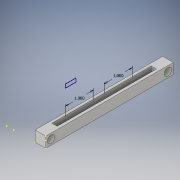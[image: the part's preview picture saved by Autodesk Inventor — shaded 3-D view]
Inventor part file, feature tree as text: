
AUTODESK INVENTOR PART (.ipt)
format: ipt  version: 2018 (Build 220112000, 112)  size: 350,208 bytes
history: native  units: in
note: dims shown in document units (in); Inventor stores cm internally (conversion verified against a paired STEP export)
features: sketch x21, extrude x11, fillet x2, hole x1
ambient origin geometry x8: Origin, YZ Plane, XZ Plane, XY Plane, X Axis, Y Axis, Z Axis, Center Point
bodies: Solid1 (feature_tree)
feature tree (35):
  extrude  "Extrusion1"  Depth=4.5in
  sketch  "Sketch2"  dims[d2=0.375in d3=0.0in d4=0.1875in]
  extrude  "Extrusion2"  Depth=0.1875in
  extrude  "Extrusion3"  Depth=0.375in TaperAngle=0.0deg
  sketch  "Sketch5"  dims[d10=0.325in d11=0.0in d12=0.3625in d13=0.0in]
  extrude  "Extrusion4"  Depth=0.26in
  extrude  "Extrusion5"  Depth=0.3625in TaperAngle=0.0deg
  extrude  "Extrusion6"  Depth=0.26in
  sketch  "Sketch9"  dims[d25=0.25in d26=0.0in d27=0.125in]
  sketch  "Sketch10"  dims[d28=0.125in d29=1.0in]
  extrude  "Extrusion7"  Depth=0.375in
  sketch  "Sketch12"  dims[d33=0.25in d34=0.75in d35=0.375in d36=0.25in d37=0.5635in d38=0.12in d39=0.8108in]
  extrude  "Extrusion8"  Depth=0.75in TaperAngle=0.0deg
  fillet  "Fillet1"  Radius=0.25in
  fillet  "Fillet2"  Radius=0.25in
  sketch  "Sketch14"  dims[d42=0.5in d43=0.0in]
  sketch  "Sketch15"
  sketch  "Sketch16"
  sketch  "Sketch17"
  sketch  "Sketch18"
  sketch  "Sketch19"
  extrude  "Extrusion9"  Depth=0.125in
  hole  "Hole1"  [1 undecoded]
  extrude  "Extrusion10"  Depth=0.125in TaperAngle=0.0deg
  extrude  "Extrusion11"  Depth=0.375in
  sketch  "Sketch1"  dims[d0=0.375in d1=4.5in]
  sketch  "Sketch3"  dims[d5=3.5in d6=0.375in d7=0.0in]
  sketch  "Sketch4"  dims[d8=0.25in d9=0.26in]
  sketch  "Sketch6"  dims[d14=0.26in d15=0.26in]
  sketch  "Sketch7"  dims[d16=0.3in d17=0.0in d18=0.375in]
  sketch  "Sketch8"  dims[d19=0.125in d20=0.75in d21=0.0in d22=0.25in d23=0.0in d24=0.25in]
  sketch  "Sketch11"  dims[d30=1.0in d31=0.125in d32=0.0in]
  sketch  "Sketch13"  dims[d40=1.0in d41=0.0in]
  sketch  "Sketch20"
  sketch  "Sketch21"
note: 1 required parameter value undecoded (feature->parameter linkage not recoverable at this tier; creation-order binding heuristic only, values carry confidence <= 0.55)
